# Revit family: IS_SlimlineII_B8586_BIM_DE
name_source: partatom
category: Plumbing Fixtures
revit_build: Autodesk Revit MEP 2014 (Build: 20130308_1515(x64)
units: mm (PartAtom-declared; Revit-internal decimal feet)

## types (1)
- B8586AA - Slimline 2 single lever shower mixer exposed
    Accessories = www.idealstandard.de\ersatzteile
    AreaUnits = millimeters
    Assembly Code = C1030200
    AssetType = Fixed
    BIMObjectName = ISI_IdealStandard_WashBasinTaps_Slimline2_B8586AA
    BarCode = 3800861010517
    Brand = Ideal Standard
    CWFU = 0
    CodePerformance = EN 817, DIN 4109, Gruppe 1
    Color = chrome
    ConnectionType = Plumbing
    Cost = 0 $
    Default Elevation = 800 mm  [stored 2.62467 ft]
    Description = B8586AA Slimline 2 single lever shower mixer exposed
    DurationUnit = year
    ExpectedLife = 25
    FaucetFunction = MIXED
    FaucetOperation = LEVERHANDLE
    FaucetType = PILLAR
    Features = Slimline 2 single lever shower mixer exposed
    Finish = chrome
    FlowRate = 15 L/min @ 3bar
    GrossWeight = 0
    HWFU = 0
    IfcExportAs = IfcValveType
    IfcExportType = FAUCET
    InstallationInstructions = www.idealstandard.de\produkte
    LinearUnits = millimeters
    ManufacturerURL = www.idealstandard.de
    Material = Brass
    Model = B8586AA
    ModelNumber = B8586AA
    ModelReference = B8586AA Slimline 2 single lever shower mixer exposed
    NBSDescription = Water supply fittings for wash basins and troughs
    NBSReference = 45-35-70/371
    Name = WashBasinTaps_Slimline2_B8586AA_IdealStandard
    NettWeight = 1,3 kg
    NominalHeight = 119 mm
    NominalLength = 133 mm
    NominalWidth = 220 mm
    ProductInformation = www.idealstandard.de/produkte
    Shape = Sculptured
    Size = 185x190x150mm
    Space = Internal
    SpareParts = www.idealstandard.de/ersatzteile
    TMV3 = No
    TestPressure = 10 Bar
    URL = www.idealstandard.com
    Uniclass2015Code = Pr_40_20_87_98
    Uniclass2015Title = Wash basin taps
    Uniclass2015Version = Products v1.1
    ValveOperation = i.e.lever
    Version = 2
    VolumeUnits = Litres
    WFU = 0
    WarrantyDescription = Manufacturers Warranty
    WarrantyDurationUnit = year
    WorkingPressure = 0

note: [stored X ft] marks values corroborated as IEEE doubles in the binary element streams (Revit-internal decimal feet)

## geometry (parser evidence)
native form markers: Sweep x2
no freeform markers — native parametric forms only
